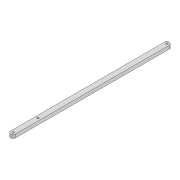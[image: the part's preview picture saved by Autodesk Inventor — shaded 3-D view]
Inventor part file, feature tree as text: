
AUTODESK INVENTOR PART (.ipt)
format: ipt  version: 2022 (Build 260153000, 153)  size: 93,184 bytes
history: native  units: mm
features: extrude x1, sketch x1
ambient origin geometry x8: Origin, YZ Plane, XZ Plane, XY Plane, X Axis, Y Axis, Z Axis, Center Point
bodies: Solid1 (feature_tree)
feature tree (2):
  extrude  "Extrusion1"  Depth=29.054mm
  sketch  "Sketch1"  dims[d0=2.2mm d1=2.2mm d2=6.0mm d3=180.271mm d6=4.0mm d7=0.0mm d14=2.2mm d15=29.054mm]
